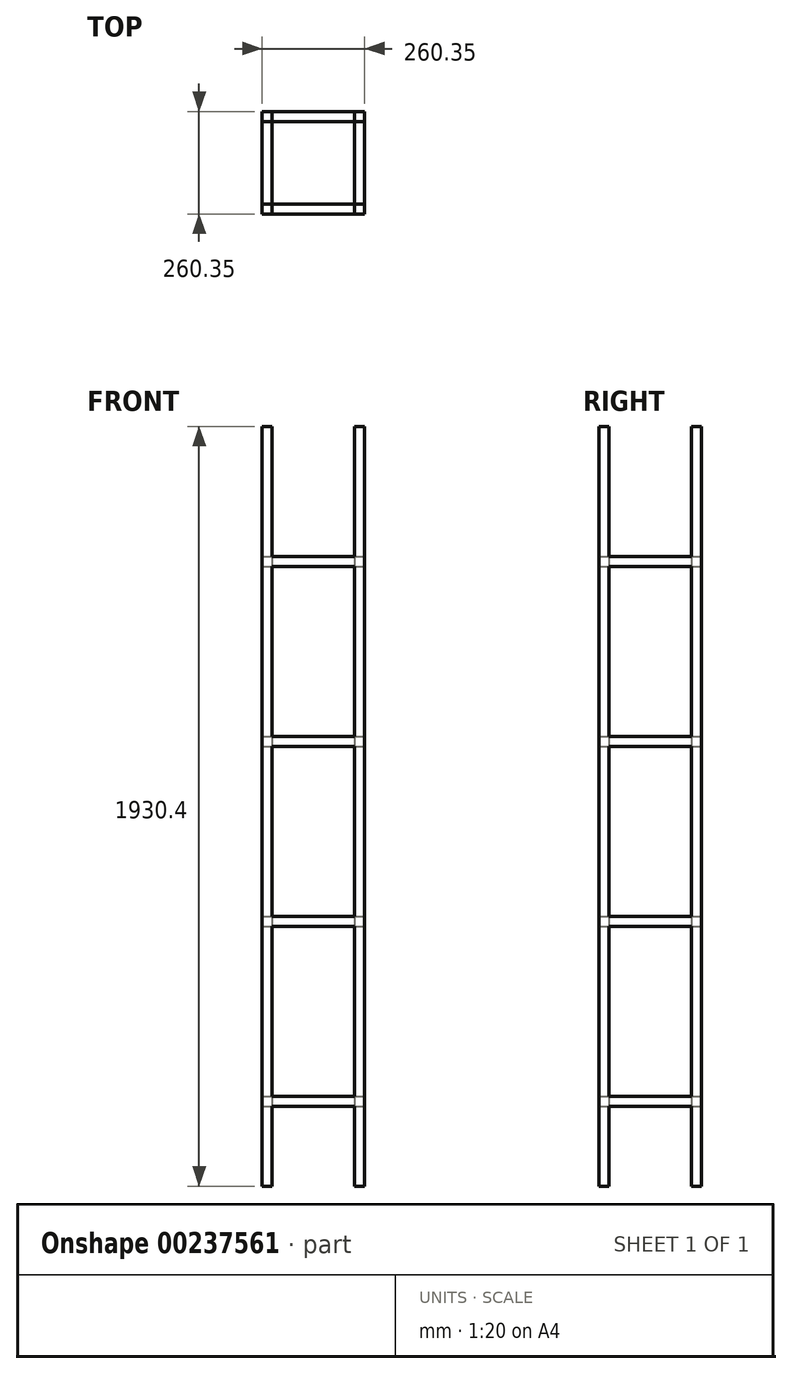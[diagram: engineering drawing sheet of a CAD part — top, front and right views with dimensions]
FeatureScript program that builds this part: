
annotation { "Feature Type Name" : "Feature", "Feature Type Description" : "" }
export const myFeature = defineFeature(function(context is Context, id is Id, definition is map)
    precondition{}
    {
        {
            var Q0;
            Q0=qCreatedBy(makeId("Top.planeOp"),FACE);
            var sketch = newSketch(context, id + "F0", { "sketchPlane" : qUnion([Q0])});
            skLineSegment(sketch, "E0.bottom", {"start": v(0, 0) * mm, "end": v(139.7, 0) * mm});
            skLineSegment(sketch, "E0.top", {"start": v(0, 139.7) * mm, "end": v(139.7, 139.7) * mm});
            skLineSegment(sketch, "E0.left", {"start": v(0, 0) * mm, "end": v(0, 139.7) * mm});
            skLineSegment(sketch, "E0.right", {"start": v(139.7, 0) * mm, "end": v(139.7, 139.7) * mm});
            skLineSegment(sketch, "E1.bottom", {"start": v(-34.92, -34.93) * mm, "end": v(174.63, -34.93) * mm});
            skLineSegment(sketch, "E1.top", {"start": v(-34.93, 174.63) * mm, "end": v(174.62, 174.63) * mm});
            skLineSegment(sketch, "E1.left", {"start": v(-34.92, -34.92) * mm, "end": v(-34.93, 174.63) * mm});
            skLineSegment(sketch, "E1.right", {"start": v(174.63, -34.92) * mm, "end": v(174.62, 174.63) * mm});
            skLineSegment(sketch, "E2.bottom", {"start": v(-60.33, 200.03) * mm, "end": v(200.03, 200.03) * mm});
            skLineSegment(sketch, "E2.top", {"start": v(-60.33, -60.33) * mm, "end": v(200.03, -60.33) * mm});
            skLineSegment(sketch, "E2.left", {"start": v(-60.33, 200.03) * mm, "end": v(-60.33, -60.33) * mm});
            skLineSegment(sketch, "E2.right", {"start": v(200.02, 200.03) * mm, "end": v(200.03, -60.33) * mm});
            skSolve(sketch);
        }
        {
            var Q0;
            Q0=makeQuery(id+"F0.imprint","IMPRINT",FACE,{"disambiguationData":[TD([[makeQuery(id+"F0.imprint","IMPRINT",EDGE,{"derivedFrom":sQuery(id+"F0.wireOp",EDGE,"E1.bottom")}),-1.0]])]});
            extrude(context, id + "F1", {"entities" : qUnion([Q0]), "depth" : 1930.4 * mm});
        }
        {
            var Q0;
            Q0=makeQuery(id+"F1.opExtrude","SWEPT_FACE",FACE,{"disambiguationData":[OSD([sQuery(id+"F0.wireOp",EDGE,"E2.right")])]});
            var sketch = newSketch(context, id + "F2", { "sketchPlane" : qUnion([Q0])});
            skLineSegment(sketch, "E3", {"start": v(-34.93, 1930.4) * mm, "end": v(-34.93, 0) * mm});
            skLineSegment(sketch, "E4", {"start": v(174.63, 0) * mm, "end": v(174.62, 1930.4) * mm});
            skLineSegment(sketch, "E5", {"start": v(-34.93, 203.2) * mm, "end": v(174.62, 203.2) * mm});
            skLineSegment(sketch, "E6", {"start": v(-34.93, 228.6) * mm, "end": v(174.62, 228.6) * mm});
            skLineSegment(sketch, "E7", {"start": v(-34.93, 660.4) * mm, "end": v(174.62, 660.4) * mm});
            skLineSegment(sketch, "E8", {"start": v(-34.93, 685.8) * mm, "end": v(174.62, 685.8) * mm});
            skLineSegment(sketch, "E9", {"start": v(-34.93, 1117.6) * mm, "end": v(174.62, 1117.6) * mm});
            skLineSegment(sketch, "E10", {"start": v(-34.93, 1143) * mm, "end": v(174.62, 1143) * mm});
            skLineSegment(sketch, "E11", {"start": v(-34.93, 1600.2) * mm, "end": v(174.62, 1600.2) * mm});
            skLineSegment(sketch, "E12", {"start": v(-34.93, 1574.8) * mm, "end": v(174.62, 1574.8) * mm});
            skLineSegment(sketch, "E13", {"start": v(-34.93, 1930.4) * mm, "end": v(174.62, 1930.4) * mm});
            skLineSegment(sketch, "E14", {"start": v(-34.93, 0) * mm, "end": v(174.63, 0) * mm});
            skSolve(sketch);
        }
        {
            var Q0;
            {var subQ3=sQuery(id+"F2.wireOp",EDGE,"E11");Q0=makeQuery(id+"F2.imprint","IMPRINT",FACE,{"disambiguationData":[TD([[makeQuery(id+"F2.imprint","IMPRINT",EDGE,{"derivedFrom":subQ3}),1.0]])]});}
            var Q1;
            {var subQ0=sQuery(id+"F2.wireOp",EDGE,"E10");Q1=makeQuery(id+"F2.imprint","IMPRINT",FACE,{"disambiguationData":[TD([[makeQuery(id+"F2.imprint","IMPRINT",EDGE,{"derivedFrom":subQ0}),1.0]])]});}
            var Q2;
            {var subQ0=sQuery(id+"F2.wireOp",EDGE,"E8");Q2=makeQuery(id+"F2.imprint","IMPRINT",FACE,{"disambiguationData":[TD([[makeQuery(id+"F2.imprint","IMPRINT",EDGE,{"derivedFrom":subQ0}),1.0]])]});}
            var Q3;
            {var subQ0=sQuery(id+"F2.wireOp",EDGE,"E6");Q3=makeQuery(id+"F2.imprint","IMPRINT",FACE,{"disambiguationData":[TD([[makeQuery(id+"F2.imprint","IMPRINT",EDGE,{"derivedFrom":subQ0}),1.0]])]});}
            var Q4;
            {var subQ3=sQuery(id+"F2.wireOp",EDGE,"E5");Q4=makeQuery(id+"F2.imprint","IMPRINT",FACE,{"disambiguationData":[TD([[makeQuery(id+"F2.imprint","IMPRINT",EDGE,{"derivedFrom":subQ3}),-1.0]])]});}
            extrude(context, id + "F3", {"entities" : qUnion([Q0, Q1, Q2, Q3, Q4]), "operationType" : NewBodyOperationType.REMOVE, "oppositeDirection" : true, "depth" : 260.35 * mm});
        }
        {
            var Q0;
            Q0=makeQuery(id+"F1.opExtrude","SWEPT_FACE",FACE,{"disambiguationData":[OSD([sQuery(id+"F0.wireOp",EDGE,"E2.bottom")])]});
            var sketch = newSketch(context, id + "F4", { "sketchPlane" : qUnion([Q0])});
            skLineSegment(sketch, "E15", {"start": v(-174.62, 1930.4) * mm, "end": v(-174.62, 0) * mm});
            skLineSegment(sketch, "E16", {"start": v(34.93, 0) * mm, "end": v(34.92, 1930.4) * mm});
            skLineSegment(sketch, "E17", {"start": v(-174.63, 1600.2) * mm, "end": v(34.93, 1600.2) * mm});
            skLineSegment(sketch, "E18", {"start": v(-174.63, 1574.8) * mm, "end": v(34.93, 1574.8) * mm});
            skLineSegment(sketch, "E19", {"start": v(-174.63, 1143) * mm, "end": v(34.93, 1143) * mm});
            skLineSegment(sketch, "E20", {"start": v(-174.63, 1117.6) * mm, "end": v(34.93, 1117.6) * mm});
            skLineSegment(sketch, "E21", {"start": v(-174.62, 685.8) * mm, "end": v(34.93, 685.8) * mm});
            skLineSegment(sketch, "E22", {"start": v(-174.62, 660.4) * mm, "end": v(34.93, 660.4) * mm});
            skLineSegment(sketch, "E23", {"start": v(-174.62, 228.6) * mm, "end": v(34.93, 228.6) * mm});
            skLineSegment(sketch, "E24", {"start": v(-174.62, 203.2) * mm, "end": v(34.93, 203.2) * mm});
            skLineSegment(sketch, "E25", {"start": v(-174.62, 1930.4) * mm, "end": v(34.92, 1930.4) * mm});
            skLineSegment(sketch, "E26", {"start": v(-174.62, 0) * mm, "end": v(34.93, 0) * mm});
            skSolve(sketch);
        }
        {
            var Q0;
            {var subQ3=sQuery(id+"F4.wireOp",EDGE,"E24");Q0=makeQuery(id+"F4.imprint","IMPRINT",FACE,{"disambiguationData":[TD([[makeQuery(id+"F4.imprint","IMPRINT",EDGE,{"derivedFrom":subQ3}),-1.0]])]});}
            var Q1;
            {var subQ0=sQuery(id+"F4.wireOp",EDGE,"E22");Q1=makeQuery(id+"F4.imprint","IMPRINT",FACE,{"disambiguationData":[TD([[makeQuery(id+"F4.imprint","IMPRINT",EDGE,{"derivedFrom":subQ0}),-1.0]])]});}
            var Q2;
            {var subQ0=sQuery(id+"F4.wireOp",EDGE,"E20");Q2=makeQuery(id+"F4.imprint","IMPRINT",FACE,{"disambiguationData":[TD([[makeQuery(id+"F4.imprint","IMPRINT",EDGE,{"derivedFrom":subQ0}),-1.0]])]});}
            var Q3;
            {var subQ0=sQuery(id+"F4.wireOp",EDGE,"E18");Q3=makeQuery(id+"F4.imprint","IMPRINT",FACE,{"disambiguationData":[TD([[makeQuery(id+"F4.imprint","IMPRINT",EDGE,{"derivedFrom":subQ0}),-1.0]])]});}
            var Q4;
            {var subQ3=sQuery(id+"F4.wireOp",EDGE,"E17");Q4=makeQuery(id+"F4.imprint","IMPRINT",FACE,{"disambiguationData":[TD([[makeQuery(id+"F4.imprint","IMPRINT",EDGE,{"derivedFrom":subQ3}),1.0]])]});}
            extrude(context, id + "F5", {"entities" : qUnion([Q0, Q1, Q2, Q3, Q4]), "operationType" : NewBodyOperationType.REMOVE, "oppositeDirection" : true, "depth" : 260.35 * mm});
        }
    });
